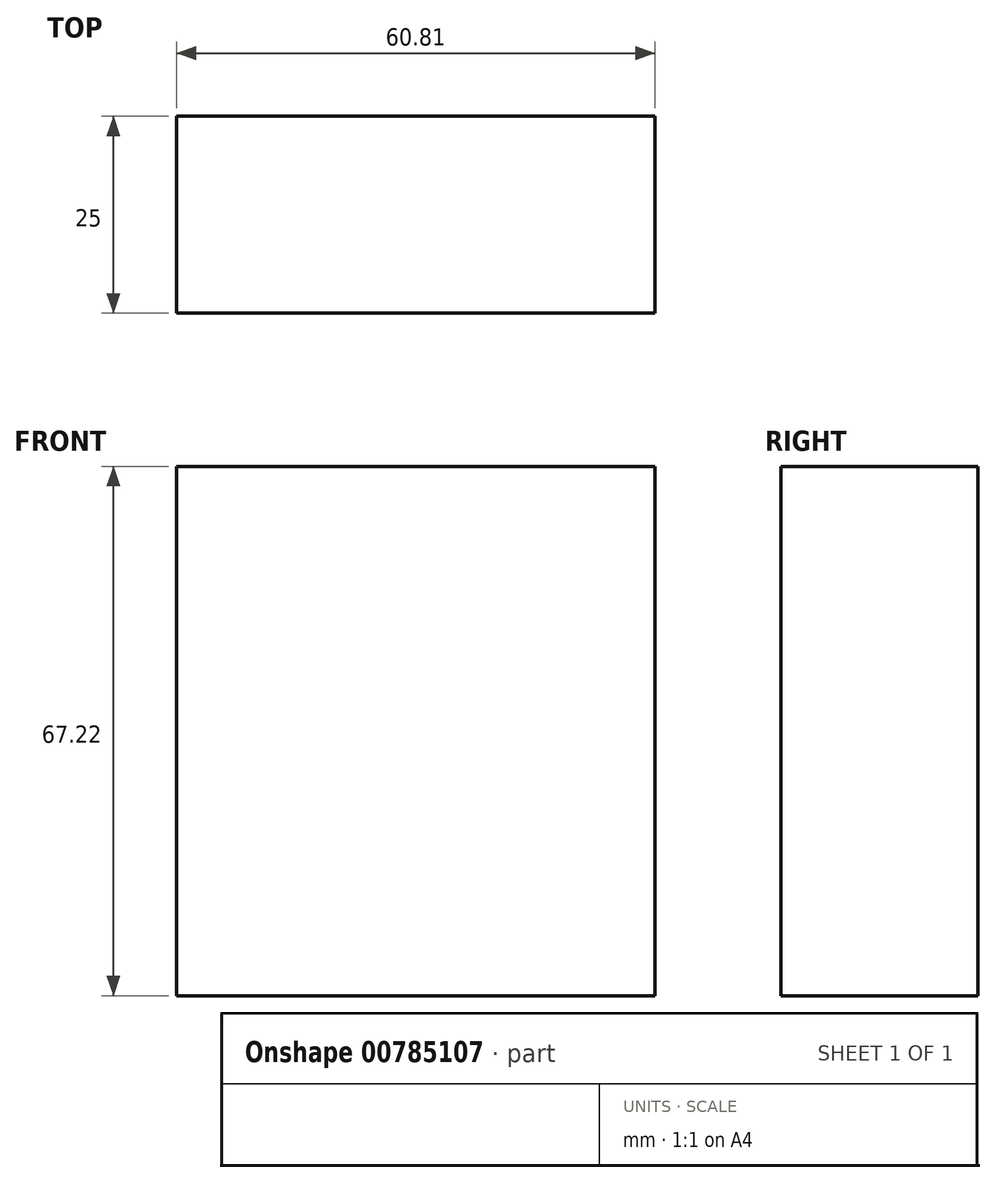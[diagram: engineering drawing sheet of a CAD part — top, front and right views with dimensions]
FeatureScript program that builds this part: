
annotation { "Feature Type Name" : "Feature", "Feature Type Description" : "" }
export const myFeature = defineFeature(function(context is Context, id is Id, definition is map)
    precondition{}
    {
        {
            var Q0;
            Q0=qCreatedBy(makeId("Front.planeOp"),FACE);
            var sketch = newSketch(context, id + "F0", { "sketchPlane" : qUnion([Q0])});
            skLineSegment(sketch, "E0.bottom", {"start": v(0, 67.22) * mm, "end": v(60.8, 67.22) * mm});
            skLineSegment(sketch, "E0.left", {"start": v(0, 67.22) * mm, "end": v(0, 62.09) * mm});
            skLineSegment(sketch, "E0.right", {"start": v(60.8, 67.22) * mm, "end": v(60.8, 62.09) * mm});
            skLineSegment(sketch, "E1.left", {"start": v(0, 62.09) * mm, "end": v(0, 53.83) * mm});
            skLineSegment(sketch, "E1.right", {"start": v(60.8, 62.09) * mm, "end": v(60.8, 53.83) * mm});
            skLineSegment(sketch, "E2.left", {"start": v(60.8, 53.83) * mm, "end": v(60.8, 50.72) * mm});
            skLineSegment(sketch, "E2.right", {"start": v(0, 53.83) * mm, "end": v(0, 50.72) * mm});
            skLineSegment(sketch, "E3.top", {"start": v(0, 0) * mm, "end": v(60.8, 0) * mm});
            skLineSegment(sketch, "E3.left", {"start": v(0, 50.72) * mm, "end": v(0, 0) * mm});
            skLineSegment(sketch, "E4", {"start": v(60.8, 42.77) * mm, "end": v(0, 42.77) * mm});
            skLineSegment(sketch, "E5", {"start": v(60.8, 50.72) * mm, "end": v(0, 50.72) * mm});
            skLineSegment(sketch, "E6", {"start": v(60.8, 32.84) * mm, "end": v(0, 32.84) * mm});
            skPoint(sketch, "E6.endSnap0", {"position": v(0, 25.36) * mm});
            skLineSegment(sketch, "E7", {"start": v(60.8, 59.67) * mm, "end": v(0, 59.67) * mm});
            skLineSegment(sketch, "E8", {"start": v(60.8, 50.72) * mm, "end": v(60.8, 0) * mm});
            skSolve(sketch);
        }
        {
            var Q0;
            Q0 = qSketchRegion(id + "F0", true);
            extrude(context, id + "F1", {"entities" : qUnion([Q0]), "depth" : 25 * mm, "offsetDistance" : 25 * mm});
        }
    });
